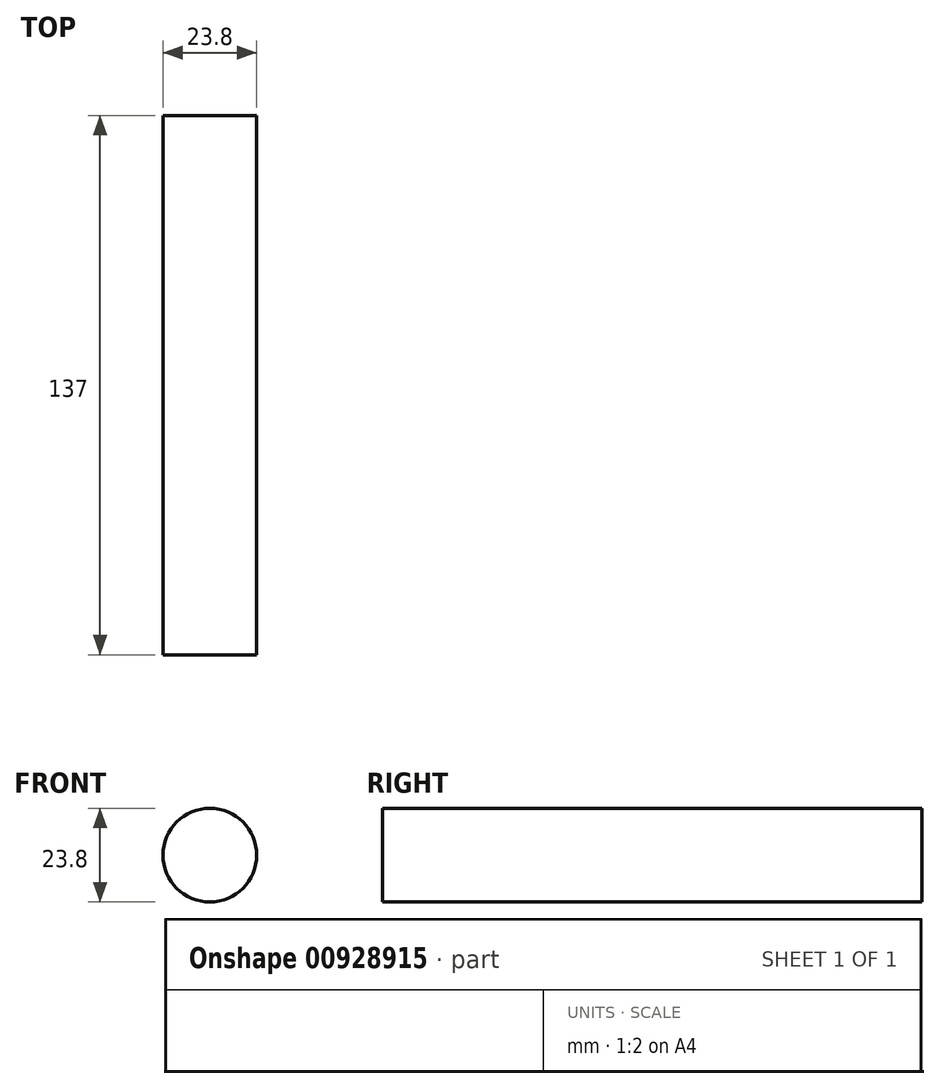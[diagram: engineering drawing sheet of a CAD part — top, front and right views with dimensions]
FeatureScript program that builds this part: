
annotation { "Feature Type Name" : "Feature", "Feature Type Description" : "" }
export const myFeature = defineFeature(function(context is Context, id is Id, definition is map)
    precondition{}
    {
        {
            var Q0;
            Q0=qCreatedBy(makeId("Front.planeOp"),FACE);
            var sketch = newSketch(context, id + "F0", { "sketchPlane" : qUnion([Q0])});
            skCircle(sketch, "E0", {"center": v(0, 0) * mm, "radius": 11.9 * mm});
            skSolve(sketch);
        }
        {
            var Q0;
            Q0=makeQuery(id+"F0.imprint","IMPRINT",FACE,{"disambiguationData":[TD([[makeQuery(id+"F0.imprint","IMPRINT",EDGE,{"derivedFrom":sQuery(id+"F0.wireOp",EDGE,"E0")}),1.0]])]});
            extrude(context, id + "F1", {"entities" : qUnion([Q0]), "depth" : 137 * mm, "offsetDistance" : 25 * mm});
        }
    });
